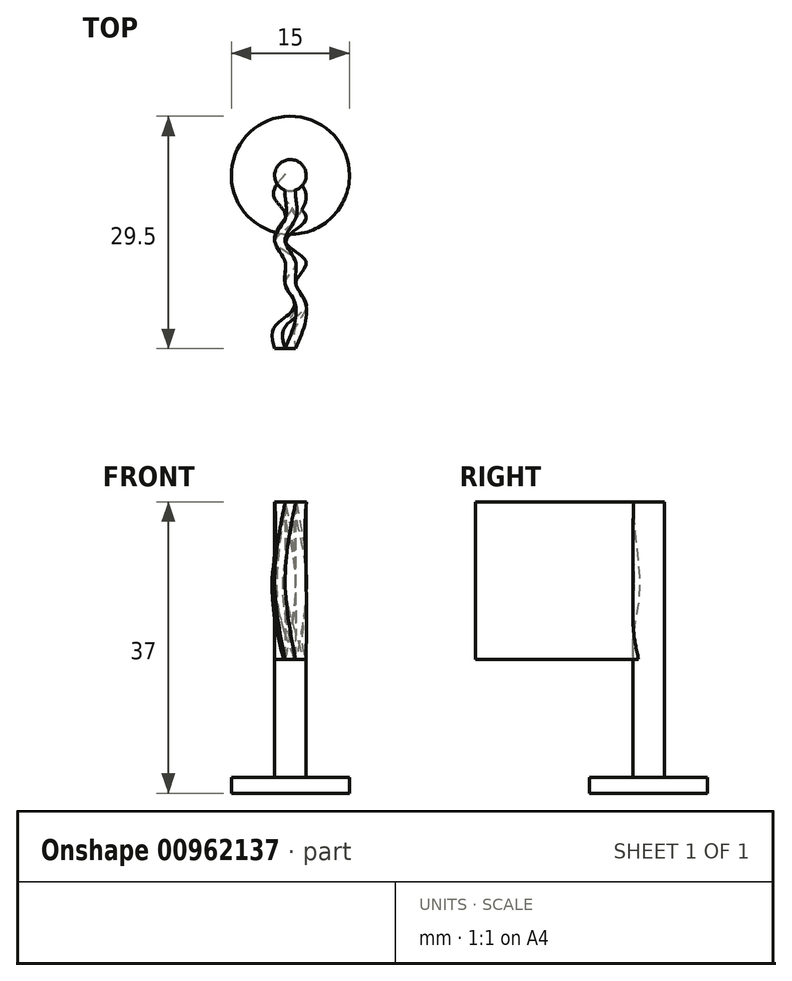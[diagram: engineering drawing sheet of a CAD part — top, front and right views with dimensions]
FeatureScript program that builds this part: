
annotation { "Feature Type Name" : "Feature", "Feature Type Description" : "" }
export const myFeature = defineFeature(function(context is Context, id is Id, definition is map)
    precondition{}
    {
        {
            var Q0;
            Q0=qCreatedBy(makeId("Top.planeOp"),FACE);
            var sketch = newSketch(context, id + "F0", { "sketchPlane" : qUnion([Q0])});
            skCircle(sketch, "E0", {"center": v(0, 0) * mm, "radius": 7.5 * mm});
            skSolve(sketch);
        }
        {
            var Q0;
            Q0=makeQuery(id+"F0.imprint","IMPRINT",FACE,{"disambiguationData":[TD([[makeQuery(id+"F0.imprint","IMPRINT",EDGE,{"derivedFrom":sQuery(id+"F0.wireOp",EDGE,"E0")}),1.0]])]});
            extrude(context, id + "F1", {"entities" : qUnion([Q0]), "depth" : 2 * mm, "offsetDistance" : 25 * mm});
        }
        {
            var Q0;
            Q0=makeQuery(id+"F1.opExtrude","CAP_FACE",FACE,{"disambiguationData":[OSD([sQuery(id+"F0.wireOp",EDGE,"E0")])],"isStart":false});
            var sketch = newSketch(context, id + "F2", { "sketchPlane" : qUnion([Q0])});
            skCircle(sketch, "E1", {"center": v(0, 0) * mm, "radius": 2 * mm});
            skSolve(sketch);
        }
        {
            var Q0;
            Q0=makeQuery(id+"F2.imprint","IMPRINT",FACE,{"disambiguationData":[TD([[makeQuery(id+"F2.imprint","IMPRINT",EDGE,{"derivedFrom":sQuery(id+"F2.wireOp",EDGE,"E1")}),1.0]])]});
            extrude(context, id + "F3", {"entities" : qUnion([Q0]), "operationType" : NewBodyOperationType.ADD, "depth" : 35 * mm, "offsetDistance" : 25 * mm});
        }
        {
            var Q0;
            Q0=makeQuery(id+"F1.opExtrude","CAP_FACE",FACE,{"disambiguationData":[OSD([sQuery(id+"F0.wireOp",EDGE,"E0")])],"isStart":false});
            cPlane(context, id + "F4", {"entities" : qUnion([Q0]), "cplaneType" : CPlaneType.OFFSET, "offset" : 15 * mm, "width" : 150 * mm, "height" : 150 * mm});
        }
        {
            var Q0;
            Q0=qCreatedBy(id+"F4.planeOp",FACE);
            cPlane(context, id + "F5", {"entities" : qUnion([Q0]), "cplaneType" : CPlaneType.OFFSET, "offset" : 10 * mm, "width" : 150 * mm, "height" : 150 * mm});
        }
        {
            var Q0;
            Q0=qCreatedBy(id+"F4.planeOp",FACE);
            var sketch = newSketch(context, id + "F6", { "sketchPlane" : qUnion([Q0])});
            skCircle(sketch, "E2.0.0", {"center": v(0, 0) * mm, "radius": 2 * mm, "construction": true});
            skLineSegment(sketch, "E3", {"start": v(0, 0) * mm, "end": v(2, 0) * mm, "construction": true});
            skLineSegment(sketch, "E4", {"start": v(0, 0) * mm, "end": v(-2, 0) * mm, "construction": true});
            skLineSegment(sketch, "E5", {"start": v(-2, 0) * mm, "end": v(-2, -22) * mm, "construction": true});
            skLineSegment(sketch, "E6", {"start": v(-2, -22) * mm, "end": v(2, -22) * mm, "construction": true});
            skLineSegment(sketch, "E7", {"start": v(2, -22) * mm, "end": v(2, 0) * mm, "construction": true});
            skLineSegment(sketch, "E8", {"start": v(0.67, -22) * mm, "end": v(0.67, 0) * mm, "construction": true});
            skLineSegment(sketch, "E9", {"start": v(-2, -11) * mm, "end": v(-0.67, -11) * mm, "construction": true});
            skLineSegment(sketch, "E10", {"start": v(-0.67, -11) * mm, "end": v(0.67, -11) * mm, "construction": true});
            skLineSegment(sketch, "E11", {"start": v(0.67, -11) * mm, "end": v(2, -11) * mm, "construction": true});
            skPoint(sketch, "E12", {"position": v(-2, -5.5) * mm});
            skPoint(sketch, "E13", {"position": v(-0.67, -5.5) * mm});
            skPoint(sketch, "E14", {"position": v(0.67, -5.5) * mm});
            skPoint(sketch, "E15", {"position": v(2, -5.5) * mm});
            skPoint(sketch, "E16", {"position": v(-2, -16.5) * mm});
            skPoint(sketch, "E17", {"position": v(-0.67, -16.5) * mm});
            skPoint(sketch, "E18", {"position": v(0.67, -16.5) * mm});
            skPoint(sketch, "E19", {"position": v(2, -16.5) * mm});
            skPoint(sketch, "E20", {"position": v(-2, -13.75) * mm});
            skPoint(sketch, "E21", {"position": v(-0.67, -13.75) * mm});
            skPoint(sketch, "E22", {"position": v(0.67, -13.75) * mm});
            skPoint(sketch, "E23", {"position": v(2, -13.75) * mm});
            skPoint(sketch, "E24", {"position": v(2, -19.25) * mm});
            skPoint(sketch, "E25", {"position": v(0.67, -19.25) * mm});
            skPoint(sketch, "E26", {"position": v(-0.67, -19.25) * mm});
            skPoint(sketch, "E27", {"position": v(-2, -19.25) * mm});
            skPoint(sketch, "E28", {"position": v(-2, -8.25) * mm});
            skPoint(sketch, "E29", {"position": v(-0.67, -8.25) * mm});
            skPoint(sketch, "E30", {"position": v(0.67, -8.25) * mm});
            skPoint(sketch, "E31", {"position": v(2, -8.25) * mm});
            skPoint(sketch, "E32", {"position": v(2, -2.75) * mm});
            skPoint(sketch, "E33", {"position": v(0.67, -2.75) * mm});
            skPoint(sketch, "E34", {"position": v(-0.67, -2.75) * mm});
            skPoint(sketch, "E35", {"position": v(-2, -2.75) * mm});
            skLineSegment(sketch, "E36", {"start": v(-0.67, -19.25) * mm, "end": v(-0.67, -16.5) * mm, "construction": true});
            skLineSegment(sketch, "E37", {"start": v(-0.67, -19.25) * mm, "end": v(-0.67, -22) * mm, "construction": true});
            skLineSegment(sketch, "E38", {"start": v(-0.67, -16.5) * mm, "end": v(-0.67, -13.75) * mm, "construction": true});
            skLineSegment(sketch, "E39", {"start": v(-0.67, -11) * mm, "end": v(-0.67, -8.25) * mm, "construction": true});
            skLineSegment(sketch, "E40", {"start": v(-0.67, -5.5) * mm, "end": v(-0.67, -2.75) * mm, "construction": true});
            skLineSegment(sketch, "E41", {"start": v(-0.67, -2.75) * mm, "end": v(-0.67, 0) * mm, "construction": true});
            skLineSegment(sketch, "E42", {"start": v(-0.67, -5.5) * mm, "end": v(-0.67, -8.25) * mm, "construction": true});
            skLineSegment(sketch, "E43", {"start": v(-0.67, -11) * mm, "end": v(-0.67, -13.75) * mm, "construction": true});
            skFitSpline(sketch, "E44", {"points": [v(-0.67, 0) * mm, v(0.67, -2.75) * mm, v(-0.67, -5.5) * mm, v(-2, -8.25) * mm, v(-0.67, -11) * mm, v(-0.67, -13.75) * mm, v(0.67, -16.5) * mm, v(-0.67, -19.25) * mm, v(-0.67, -22) * mm], "startDerivative": vector(15.66, -20.02) * mm, "endDerivative": vector(4.49, -21.57) * mm});
            skFitSpline(sketch, "E45", {"points": [v(0.67, 0) * mm, v(2, -2.75) * mm, v(0.67, -5.5) * mm, v(-0.67, -8.25) * mm, v(0.67, -11) * mm, v(0.67, -13.75) * mm, v(2, -16.5) * mm, v(0.67, -19.25) * mm, v(0.67, -22) * mm], "startDerivative": vector(15.66, -20.02) * mm, "endDerivative": vector(4.49, -21.57) * mm});
            skLineSegment(sketch, "E46", {"start": v(-0.67, -22) * mm, "end": v(0.67, -22) * mm});
            skLineSegment(sketch, "E47", {"start": v(-0.67, 0) * mm, "end": v(0.67, 0) * mm});
            skSolve(sketch);
        }
        {
            var Q0;
            Q0=qCreatedBy(id+"F5.planeOp",FACE);
            var sketch = newSketch(context, id + "F7", { "sketchPlane" : qUnion([Q0])});
            skLineSegment(sketch, "E48.0", {"start": v(2, -22) * mm, "end": v(2, 0) * mm, "construction": true});
            skLineSegment(sketch, "E49.0", {"start": v(-0.67, -5.5) * mm, "end": v(-0.67, -2.75) * mm, "construction": true});
            skLineSegment(sketch, "E49.1", {"start": v(-0.67, -11) * mm, "end": v(-0.67, -8.25) * mm, "construction": true});
            skLineSegment(sketch, "E49.2", {"start": v(-2, -22) * mm, "end": v(2, -22) * mm, "construction": true});
            skLineSegment(sketch, "E49.3", {"start": v(-0.67, -2.75) * mm, "end": v(-0.67, 0) * mm, "construction": true});
            skLineSegment(sketch, "E49.5", {"start": v(-2, 0) * mm, "end": v(-2, -22) * mm, "construction": true});
            skLineSegment(sketch, "E49.6", {"start": v(0.67, -11) * mm, "end": v(2, -11) * mm, "construction": true});
            skLineSegment(sketch, "E49.7", {"start": v(-2, -11) * mm, "end": v(-0.67, -11) * mm, "construction": true});
            skLineSegment(sketch, "E49.8", {"start": v(-0.67, -16.5) * mm, "end": v(-0.67, -13.75) * mm, "construction": true});
            skLineSegment(sketch, "E49.9", {"start": v(-0.67, -5.5) * mm, "end": v(-0.67, -8.25) * mm, "construction": true});
            skLineSegment(sketch, "E49.10", {"start": v(-0.67, -19.25) * mm, "end": v(-0.67, -16.5) * mm, "construction": true});
            skFitSpline(sketch, "E49.11", {"points": [v(-0.67, 0) * mm, v(0, -0.85) * mm, v(1.32, -2.54) * mm, v(-0.61, -5.07) * mm, v(-2.87, -7.63) * mm, v(0.03, -10.05) * mm, v(-1.4, -12.8) * mm, v(1.68, -15.23) * mm, v(-1.21, -17.68) * mm, v(-0.85, -19.45) * mm, v(-0.67, -20.31) * mm], "construction": true});
            skLineSegment(sketch, "E49.12", {"start": v(-0.67, -19.25) * mm, "end": v(-0.67, -22) * mm, "construction": true});
            skLineSegment(sketch, "E49.13", {"start": v(-0.67, -11) * mm, "end": v(-0.67, -13.75) * mm, "construction": true});
            skLineSegment(sketch, "E50.0", {"start": v(0.67, -22) * mm, "end": v(0.67, 0) * mm, "construction": true});
            skLineSegment(sketch, "E51.0", {"start": v(-0.67, -11) * mm, "end": v(0.67, -11) * mm, "construction": true});
            skPoint(sketch, "E52.0", {"position": v(-2, -13.75) * mm});
            skPoint(sketch, "E53.0", {"position": v(-2, -16.5) * mm});
            skPoint(sketch, "E54.0", {"position": v(-2, -19.25) * mm});
            skPoint(sketch, "E55.0", {"position": v(0.67, -19.25) * mm});
            skPoint(sketch, "E56.0", {"position": v(0.67, -16.5) * mm});
            skPoint(sketch, "E57.0", {"position": v(0.67, -13.75) * mm});
            skPoint(sketch, "E58.0", {"position": v(2, -13.75) * mm});
            skPoint(sketch, "E59.0", {"position": v(2, -16.5) * mm});
            skPoint(sketch, "E60.0", {"position": v(2, -19.25) * mm});
            skPoint(sketch, "E61.0", {"position": v(-2, -8.25) * mm});
            skPoint(sketch, "E62.0", {"position": v(-0.67, -8.25) * mm});
            skPoint(sketch, "E63.0", {"position": v(0.67, -8.25) * mm});
            skPoint(sketch, "E64.0", {"position": v(2, -8.25) * mm});
            skPoint(sketch, "E65.0", {"position": v(2, -5.5) * mm});
            skPoint(sketch, "E66.0", {"position": v(0.67, -5.5) * mm});
            skPoint(sketch, "E67.0", {"position": v(-0.67, -5.5) * mm});
            skPoint(sketch, "E68.0", {"position": v(-2, -5.5) * mm});
            skPoint(sketch, "E69.0", {"position": v(-2, -2.75) * mm});
            skPoint(sketch, "E70.0", {"position": v(-0.67, -2.75) * mm});
            skPoint(sketch, "E71.0", {"position": v(0.67, -2.75) * mm});
            skPoint(sketch, "E72.0", {"position": v(2, -2.75) * mm});
            skLineSegment(sketch, "E73", {"start": v(-0.67, 0) * mm, "end": v(0.67, 0) * mm});
            skLineSegment(sketch, "E74", {"start": v(-0.67, -22) * mm, "end": v(0.67, -22) * mm});
            skFitSpline(sketch, "E75", {"points": [v(-0.67, 0) * mm, v(-2, -2.75) * mm, v(0.67, -5.5) * mm, v(-2, -8.25) * mm, v(0.67, -11) * mm, v(-0.67, -13.75) * mm, v(0.67, -16.5) * mm, v(-2, -19.25) * mm, v(-2, -22) * mm], "startDerivative": vector(-22.8, -22.16) * mm, "endDerivative": vector(7.71, -23.98) * mm});
            skFitSpline(sketch, "E76", {"points": [v(0.67, 0) * mm, v(-0.67, -2.75) * mm, v(2, -5.5) * mm, v(-0.67, -8.25) * mm, v(2, -11) * mm, v(0.67, -13.75) * mm, v(2, -16.5) * mm, v(-0.67, -19.25) * mm, v(-0.67, -22) * mm], "startDerivative": vector(-22.8, -22.16) * mm, "endDerivative": vector(7.71, -23.98) * mm});
            skLineSegment(sketch, "E77", {"start": v(-0.67, -22) * mm, "end": v(-2, -22) * mm});
            skSolve(sketch);
        }
        {
            var Q0;
            Q0=makeQuery(id+"F3.opExtrude","CAP_FACE",FACE,{"disambiguationData":[OSD([sQuery(id+"F2.wireOp",EDGE,"E1")])],"isStart":false});
            var sketch = newSketch(context, id + "F8", { "sketchPlane" : qUnion([Q0])});
            skLineSegment(sketch, "E78.0", {"start": v(0.67, -22) * mm, "end": v(0.67, 0) * mm, "construction": true});
            skLineSegment(sketch, "E78.1", {"start": v(-0.67, -11) * mm, "end": v(-0.67, -8.25) * mm, "construction": true});
            skLineSegment(sketch, "E78.2", {"start": v(0, 0) * mm, "end": v(2, 0) * mm, "construction": true});
            skCircle(sketch, "E78.3", {"center": v(0, 0) * mm, "radius": 2 * mm, "construction": true});
            skLineSegment(sketch, "E78.4", {"start": v(-2, -22) * mm, "end": v(2, -22) * mm, "construction": true});
            skLineSegment(sketch, "E78.5", {"start": v(-0.67, -22) * mm, "end": v(0.67, -22) * mm, "construction": true});
            skLineSegment(sketch, "E78.6", {"start": v(-2, 0) * mm, "end": v(-2, -22) * mm, "construction": true});
            skLineSegment(sketch, "E78.7", {"start": v(0.67, -11) * mm, "end": v(2, -11) * mm, "construction": true});
            skLineSegment(sketch, "E78.8", {"start": v(-2, -11) * mm, "end": v(-0.67, -11) * mm, "construction": true});
            skLineSegment(sketch, "E78.9", {"start": v(2, -22) * mm, "end": v(2, 0) * mm, "construction": true});
            skLineSegment(sketch, "E78.10", {"start": v(-0.67, -11) * mm, "end": v(0.67, -11) * mm, "construction": true});
            skLineSegment(sketch, "E78.11", {"start": v(0, 0) * mm, "end": v(-2, 0) * mm, "construction": true});
            skLineSegment(sketch, "E78.14", {"start": v(-0.67, -19.25) * mm, "end": v(-0.67, -22) * mm, "construction": true});
            skLineSegment(sketch, "E78.16", {"start": v(2, -22) * mm, "end": v(2, 0) * mm, "construction": true});
            skLineSegment(sketch, "E78.17", {"start": v(-0.67, -2.75) * mm, "end": v(-0.67, 0) * mm, "construction": true});
            skLineSegment(sketch, "E78.18", {"start": v(-2, -11) * mm, "end": v(-0.67, -11) * mm, "construction": true});
            skLineSegment(sketch, "E78.20", {"start": v(-2, 0) * mm, "end": v(-2, -22) * mm, "construction": true});
            skLineSegment(sketch, "E78.21", {"start": v(-0.67, -20.31) * mm, "end": v(0.67, -20.31) * mm, "construction": true});
            skLineSegment(sketch, "E78.23", {"start": v(-0.67, -16.5) * mm, "end": v(-0.67, -13.75) * mm, "construction": true});
            skLineSegment(sketch, "E78.24", {"start": v(0.67, -22) * mm, "end": v(0.67, 0) * mm, "construction": true});
            skLineSegment(sketch, "E78.25", {"start": v(-2, -22) * mm, "end": v(2, -22) * mm, "construction": true});
            skLineSegment(sketch, "E78.26", {"start": v(-0.67, 0) * mm, "end": v(0.67, 0) * mm, "construction": true});
            skLineSegment(sketch, "E78.27", {"start": v(0.67, -11) * mm, "end": v(2, -11) * mm, "construction": true});
            skLineSegment(sketch, "E78.28", {"start": v(-0.67, -11) * mm, "end": v(0.67, -11) * mm, "construction": true});
            skCircle(sketch, "E78.31", {"center": v(0, 0) * mm, "radius": 2 * mm, "construction": true});
            skLineSegment(sketch, "E78.32", {"start": v(-0.67, -5.5) * mm, "end": v(-0.67, -2.75) * mm, "construction": true});
            skLineSegment(sketch, "E78.33", {"start": v(-0.67, -11) * mm, "end": v(-0.67, -13.75) * mm, "construction": true});
            skLineSegment(sketch, "E78.34", {"start": v(-0.67, -5.5) * mm, "end": v(-0.67, -8.25) * mm, "construction": true});
            skLineSegment(sketch, "E78.35", {"start": v(-0.67, -19.25) * mm, "end": v(-0.67, -16.5) * mm, "construction": true});
            skLineSegment(sketch, "E78.36", {"start": v(-0.67, 0) * mm, "end": v(0.67, 0) * mm, "construction": true});
            skLineSegment(sketch, "E78.37", {"start": v(-0.67, -5.5) * mm, "end": v(-0.67, -8.25) * mm, "construction": true});
            skLineSegment(sketch, "E78.38", {"start": v(-0.67, -2.75) * mm, "end": v(-0.67, 0) * mm, "construction": true});
            skLineSegment(sketch, "E78.39", {"start": v(-0.67, -2.75) * mm, "end": v(-0.67, 0) * mm, "construction": true});
            skFitSpline(sketch, "E79", {"points": [v(-0.67, 0) * mm, v(-0.67, -2.75) * mm, v(-0.67, -5.5) * mm, v(-2, -8.25) * mm, v(-0.67, -11) * mm, v(-0.67, -13.75) * mm, v(0.67, -16.5) * mm, v(-0.67, -22) * mm], "startDerivative": vector(-1.1, -19.3) * mm, "endDerivative": vector(-13.3, -29.71) * mm});
            skFitSpline(sketch, "E80", {"points": [v(0.67, 0) * mm, v(0.67, -2.75) * mm, v(0.67, -5.5) * mm, v(-0.67, -8.25) * mm, v(0.67, -11) * mm, v(0.67, -13.75) * mm, v(2, -16.5) * mm, v(0.67, -22) * mm], "startDerivative": vector(-1.1, -19.3) * mm, "endDerivative": vector(-13.3, -29.71) * mm});
            skLineSegment(sketch, "E81", {"start": v(-0.67, -22) * mm, "end": v(0.67, -22) * mm});
            skLineSegment(sketch, "E82", {"start": v(-0.67, 0) * mm, "end": v(0.67, 0) * mm});
            skSolve(sketch);
        }
        {
            var Q1;
            Q1=qSketchRegion(id+"F6",true);
            var Q2;
            Q2=qSketchRegion(id+"F7",true);
            var Q3;
            {var subQ0=sQuery(id+"F8.wireOp",EDGE,"E81");Q3=makeQuery(id+"F8.imprint","IMPRINT",FACE,{"disambiguationData":[TD([[makeQuery(id+"F8.imprint","IMPRINT",EDGE,{"derivedFrom":subQ0}),1.0]])]});}
            loft(context, id + "F9", {"operationType" : NewBodyOperationType.ADD, "sheetProfilesArray" : [{ "sheetProfileEntities" : qUnion([Q1]) }, { "sheetProfileEntities" : qUnion([Q2]) }, { "sheetProfileEntities" : qUnion([Q3]) }]});
        }
    });
